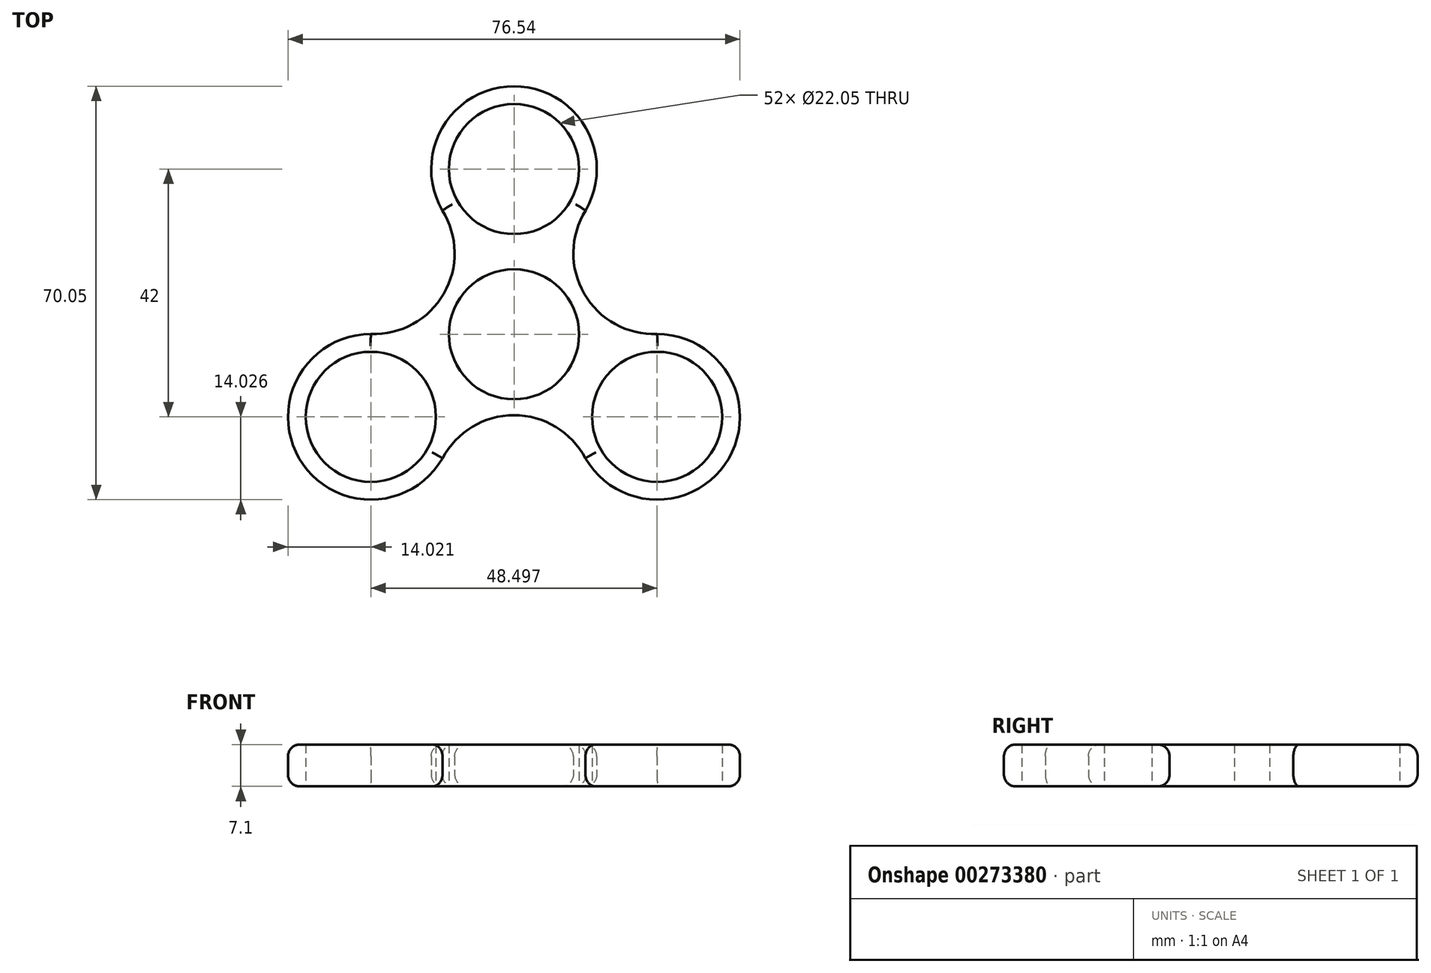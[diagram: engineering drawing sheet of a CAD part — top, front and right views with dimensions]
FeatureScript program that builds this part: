
annotation { "Feature Type Name" : "Feature", "Feature Type Description" : "" }
export const myFeature = defineFeature(function(context is Context, id is Id, definition is map)
    precondition{}
    {
        {
            var Q0;
            Q0=qCreatedBy(makeId("Top.planeOp"),FACE);
            var sketch = newSketch(context, id + "F0", { "sketchPlane" : qUnion([Q0])});
            skCircle(sketch, "E0", {"center": v(0, 23.48) * mm, "radius": 11.03 * mm});
            skCircle(sketch, "E1", {"center": v(0, -4.52) * mm, "radius": 11.03 * mm});
            skArc(sketch, "E2", {"start": v(11.88, 16.03) * mm, "mid": v(0, 37.5) * mm, "end": v(-11.88, 16.03) * mm});
            skCircle(sketch, "E3.1.0", {"center": v(-24.25, -18.52) * mm, "radius": 11.03 * mm});
            skArc(sketch, "E3.1.1", {"start": v(-23.74, -4.5) * mm, "mid": v(-36.4, -25.54) * mm, "end": v(-11.86, -25.1) * mm});
            skCircle(sketch, "E3.2.0", {"center": v(24.25, -18.52) * mm, "radius": 11.03 * mm});
            skArc(sketch, "E3.2.1", {"start": v(11.86, -25.1) * mm, "mid": v(36.4, -25.54) * mm, "end": v(23.74, -4.5) * mm});
            skLineSegment(sketch, "E4", {"start": v(0, 23.48) * mm, "end": v(-12.15, 16.46) * mm, "construction": true});
            skArc(sketch, "E5", {"start": v(-24.25, -4.5) * mm, "mid": v(-11.89, 2.34) * mm, "end": v(-12.15, 16.46) * mm});
            skArc(sketch, "E6.1.0", {"start": v(12.1, -25.54) * mm, "mid": v(0, -18.25) * mm, "end": v(-12.1, -25.54) * mm});
            skArc(sketch, "E6.2.0", {"start": v(12.15, 16.46) * mm, "mid": v(11.89, 2.34) * mm, "end": v(24.25, -4.5) * mm});
            skLineSegment(sketch, "E7", {"start": v(-24.25, -32.55) * mm, "end": v(24.25, -32.55) * mm, "construction": true});
            skCircle(sketch, "E8", {"center": v(0, -4.52) * mm, "radius": 42.03 * mm, "construction": true});
            skSolve(sketch);
        }
        {
            var Q0;
            Q0=makeQuery(id+"F0.imprint","IMPRINT",FACE,{"disambiguationData":[TD([[makeQuery(id+"F0.imprint","IMPRINT",EDGE,{"derivedFrom":sQuery(id+"F0.wireOp",EDGE,"E0")}),-1.0]])]});
            extrude(context, id + "F1", {"entities" : qUnion([Q0]), "depth" : 7.1 * mm});
        }
        {
            var Q0;
            Q0=makeQuery(id+"F1.opExtrude","CAP_EDGE",EDGE,{"disambiguationData":[OSD([sQuery(id+"F0.wireOp",EDGE,"E2")])],"isStart":false});
            var Q1;
            Q1=makeQuery(id+"F1.opExtrude","CAP_EDGE",EDGE,{"disambiguationData":[OSD([sQuery(id+"F0.wireOp",EDGE,"E3.1.1")])],"isStart":false});
            var Q2;
            Q2=makeQuery(id+"F1.opExtrude","CAP_EDGE",EDGE,{"disambiguationData":[OSD([sQuery(id+"F0.wireOp",EDGE,"E3.2.1")])],"isStart":false});
            var Q3;
            Q3=makeQuery(id+"F1.opExtrude","CAP_EDGE",EDGE,{"disambiguationData":[OSD([sQuery(id+"F0.wireOp",EDGE,"E6.1.0")])],"isStart":false});
            var Q4;
            Q4=makeQuery(id+"F1.opExtrude","CAP_EDGE",EDGE,{"disambiguationData":[OSD([sQuery(id+"F0.wireOp",EDGE,"E5")])],"isStart":false});
            var Q5;
            Q5=makeQuery(id+"F1.opExtrude","CAP_EDGE",EDGE,{"disambiguationData":[OSD([sQuery(id+"F0.wireOp",EDGE,"E6.2.0")])],"isStart":false});
            var Q6;
            Q6=makeQuery(id+"F1.opExtrude","CAP_EDGE",EDGE,{"disambiguationData":[OSD([sQuery(id+"F0.wireOp",EDGE,"E6.1.0")])],"isStart":true});
            var Q7;
            Q7=makeQuery(id+"F1.opExtrude","CAP_EDGE",EDGE,{"disambiguationData":[OSD([sQuery(id+"F0.wireOp",EDGE,"E3.1.1")])],"isStart":true});
            var Q8;
            Q8=makeQuery(id+"F1.opExtrude","CAP_EDGE",EDGE,{"disambiguationData":[OSD([sQuery(id+"F0.wireOp",EDGE,"E5")])],"isStart":true});
            var Q9;
            Q9=makeQuery(id+"F1.opExtrude","CAP_EDGE",EDGE,{"disambiguationData":[OSD([sQuery(id+"F0.wireOp",EDGE,"E2")])],"isStart":true});
            var Q10;
            Q10=makeQuery(id+"F1.opExtrude","CAP_EDGE",EDGE,{"disambiguationData":[OSD([sQuery(id+"F0.wireOp",EDGE,"E6.2.0")])],"isStart":true});
            var Q11;
            Q11=makeQuery(id+"F1.opExtrude","CAP_EDGE",EDGE,{"disambiguationData":[OSD([sQuery(id+"F0.wireOp",EDGE,"E3.2.1")])],"isStart":true});
            fillet(context, id + "F2", {"entities" : qUnion([Q0, Q1, Q2, Q3, Q4, Q5, Q6, Q7, Q8, Q9, Q10, Q11]), "radius" : 2 * mm, "tangentPropagation" : true, "allowEdgeOverflow" : false});
        }
    });
